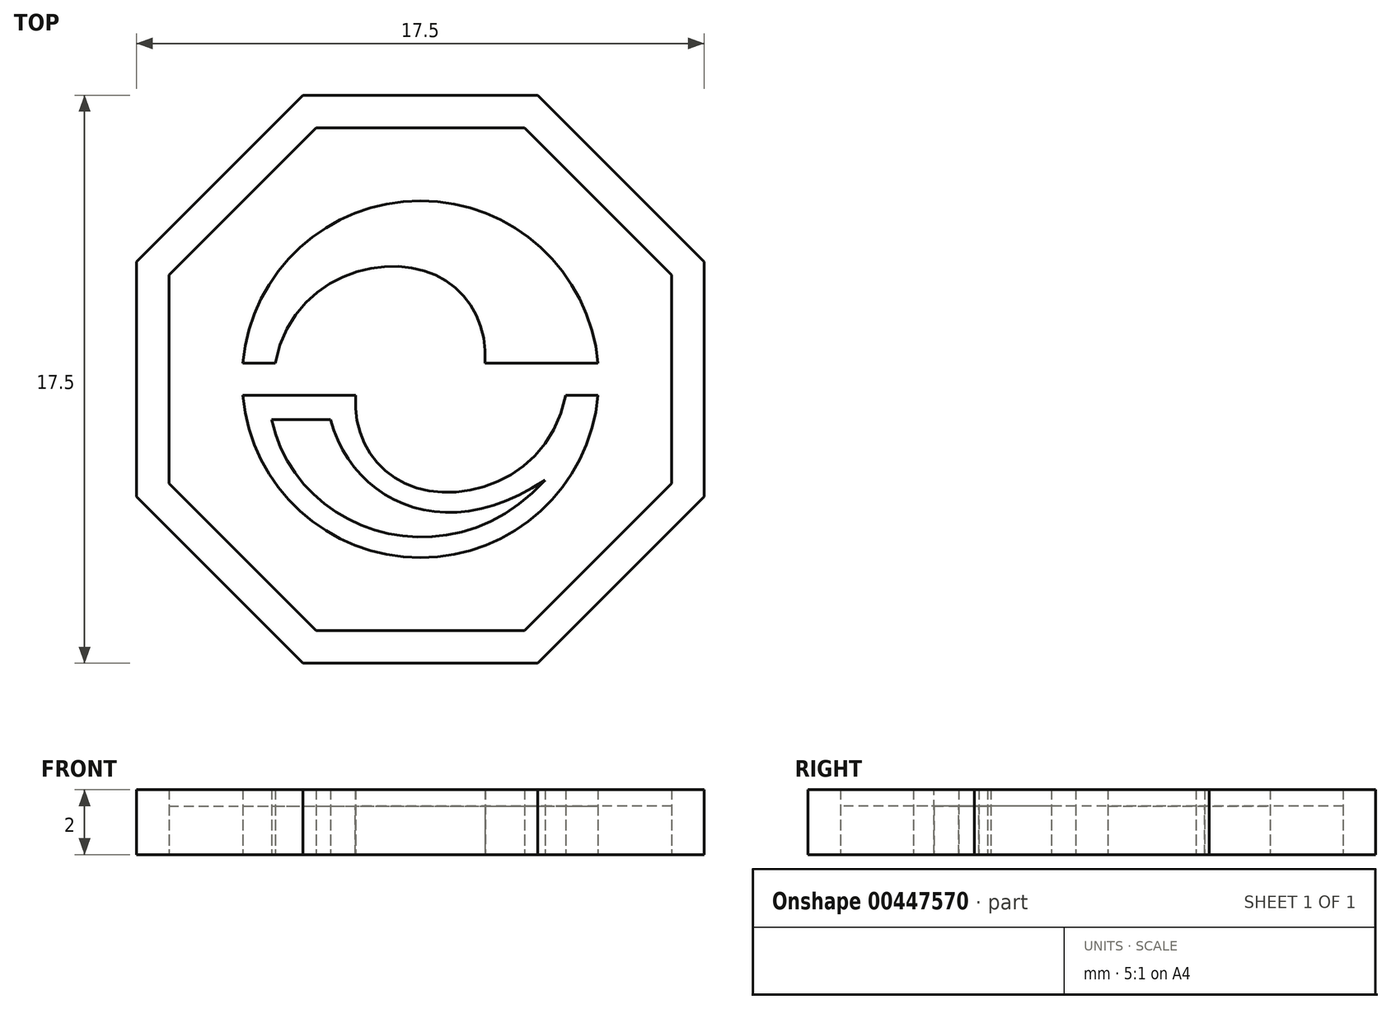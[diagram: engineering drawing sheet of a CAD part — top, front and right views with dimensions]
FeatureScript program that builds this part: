
annotation { "Feature Type Name" : "Feature", "Feature Type Description" : "" }
export const myFeature = defineFeature(function(context is Context, id is Id, definition is map)
    precondition{}
    {
        {
            var Q0;
            Q0=qCreatedBy(makeId("Top.planeOp"),FACE);
            var sketch = newSketch(context, id + "F0", { "sketchPlane" : qUnion([Q0])});
            skArc(sketch, "E0", {"start": v(-5.48, -0.5) * mm, "mid": v(0, -5.5) * mm, "end": v(5.48, -0.5) * mm});
            skLineSegment(sketch, "E1", {"start": v(-5.48, 0.5) * mm, "end": v(-4.48, 0.5) * mm});
            skLineSegment(sketch, "E2", {"start": v(-5.48, -0.5) * mm, "end": v(-2, -0.5) * mm});
            skArc(sketch, "E3.trimOffspring", {"start": v(5.48, 0.5) * mm, "mid": v(0, 5.5) * mm, "end": v(-5.48, 0.5) * mm});
            skPoint(sketch, "E4.2.internal.snap0", {"position": v(0, 0.5) * mm});
            skFitSpline(sketch, "E4", {"points": [v(-4.48, 0.5) * mm, v(0, 3.38) * mm, v(2, 0.5) * mm], "startDerivative": vector(2.69, 13.45) * mm, "endDerivative": vector(-0.52, -9.25) * mm});
            skFitSpline(sketch, "E5", {"points": [v(4.48, -0.5) * mm, v(0, -3.38) * mm, v(-2, -0.5) * mm], "startDerivative": vector(-2.69, -13.45) * mm, "endDerivative": vector(0.52, 9.25) * mm});
            skLineSegment(sketch, "E6.trimOffspring", {"start": v(2, 0.5) * mm, "end": v(5.48, 0.5) * mm});
            skLineSegment(sketch, "E7.trimOffspring", {"start": v(4.48, -0.5) * mm, "end": v(5.48, -0.5) * mm});
            skLineSegment(sketch, "E8", {"start": v(-4.58, -1.25) * mm, "end": v(-2.77, -1.25) * mm});
            skFitSpline(sketch, "E9", {"points": [v(-4.58, -1.25) * mm, v(3.85, -3.1) * mm], "startDerivative": vector(2.26, -10.5) * mm, "endDerivative": vector(8.91, 9.73) * mm});
            skFitSpline(sketch, "E10", {"points": [v(-2.77, -1.25) * mm, v(3.85, -3.1) * mm], "startDerivative": vector(2.08, -7.5) * mm, "endDerivative": vector(9.4, 6.23) * mm});
            skCircle(sketch, "E11.cCircle", {"center": v(0, 0) * mm, "radius": 7.75 * mm, "construction": true});
            skLineSegment(sketch, "E11.0", {"start": v(7.75, -3.21) * mm, "end": v(3.21, -7.75) * mm});
            skLineSegment(sketch, "E11.1", {"start": v(3.21, -7.75) * mm, "end": v(-3.21, -7.75) * mm});
            skLineSegment(sketch, "E11.2", {"start": v(-3.21, -7.75) * mm, "end": v(-7.75, -3.21) * mm});
            skLineSegment(sketch, "E11.3", {"start": v(-7.75, -3.21) * mm, "end": v(-7.75, 3.21) * mm});
            skLineSegment(sketch, "E11.4", {"start": v(-7.75, 3.21) * mm, "end": v(-3.21, 7.75) * mm});
            skLineSegment(sketch, "E11.5", {"start": v(-3.21, 7.75) * mm, "end": v(3.21, 7.75) * mm});
            skLineSegment(sketch, "E11.6", {"start": v(3.21, 7.75) * mm, "end": v(7.75, 3.21) * mm});
            skLineSegment(sketch, "E11.7", {"start": v(7.75, 3.21) * mm, "end": v(7.75, -3.21) * mm});
            skPoint(sketch, "E11.0.midPoint", {"position": v(5.48, -5.48) * mm});
            skCircle(sketch, "E12.cCircle", {"center": v(0, 0) * mm, "radius": 8.75 * mm, "construction": true});
            skLineSegment(sketch, "E12.0", {"start": v(8.75, -3.62) * mm, "end": v(3.62, -8.75) * mm});
            skLineSegment(sketch, "E12.1", {"start": v(3.62, -8.75) * mm, "end": v(-3.62, -8.75) * mm});
            skLineSegment(sketch, "E12.2", {"start": v(-3.62, -8.75) * mm, "end": v(-8.75, -3.62) * mm});
            skLineSegment(sketch, "E12.3", {"start": v(-8.75, -3.62) * mm, "end": v(-8.75, 3.62) * mm});
            skLineSegment(sketch, "E12.4", {"start": v(-8.75, 3.62) * mm, "end": v(-3.62, 8.75) * mm});
            skLineSegment(sketch, "E12.5", {"start": v(-3.62, 8.75) * mm, "end": v(3.62, 8.75) * mm});
            skLineSegment(sketch, "E12.6", {"start": v(3.62, 8.75) * mm, "end": v(8.75, 3.62) * mm});
            skLineSegment(sketch, "E12.7", {"start": v(8.75, 3.62) * mm, "end": v(8.75, -3.62) * mm});
            skPoint(sketch, "E12.0.midPoint", {"position": v(6.19, -6.19) * mm});
            skSolve(sketch);
        }
        {
            var Q0;
            Q0=makeQuery(id+"F0.imprint","IMPRINT",FACE,{"disambiguationData":[TD([[makeQuery(id+"F0.imprint","IMPRINT",EDGE,{"derivedFrom":sQuery(id+"F0.wireOp",EDGE,"62a68324-341a-4806-85d3-5feda647a868")}),1.0]])]});
            var Q1;
            Q1=makeQuery(id+"F0.imprint","IMPRINT",FACE,{"disambiguationData":[TD([[makeQuery(id+"F0.imprint","IMPRINT",EDGE,{"derivedFrom":sQuery(id+"F0.wireOp",EDGE,"E1")}),1.0]])]});
            var Q2;
            Q2=makeQuery(id+"F0.imprint","IMPRINT",FACE,{"disambiguationData":[TD([[makeQuery(id+"F0.imprint","IMPRINT",EDGE,{"derivedFrom":sQuery(id+"F0.wireOp",EDGE,"E0")}),1.0]])]});
            var Q3;
            Q3=makeQuery(id+"F0.imprint","IMPRINT",FACE,{"disambiguationData":[TD([[makeQuery(id+"F0.imprint","IMPRINT",EDGE,{"derivedFrom":sQuery(id+"F0.wireOp",EDGE,"E11.0")}),1.0]])]});
            extrude(context, id + "F1", {"entities" : qUnion([Q0, Q1, Q2, Q3]), "depth" : 2 * mm});
        }
        {
            var Q0;
            Q0=makeQuery(id+"F0.imprint","IMPRINT",FACE,{"disambiguationData":[TD([[makeQuery(id+"F0.imprint","IMPRINT",EDGE,{"derivedFrom":sQuery(id+"F0.wireOp",EDGE,"2e3d32d5-dc82-442d-8b00-b74b8bb0e9ca")}),1.0]])]});
            var Q1;
            Q1=makeQuery(id+"F0.imprint","IMPRINT",FACE,{"disambiguationData":[TD([[makeQuery(id+"F0.imprint","IMPRINT",EDGE,{"derivedFrom":sQuery(id+"F0.wireOp",EDGE,"E8")}),-1.0]])]});
            var Q2;
            Q2=makeQuery(id+"F0.imprint","IMPRINT",FACE,{"disambiguationData":[TD([[makeQuery(id+"F0.imprint","IMPRINT",EDGE,{"derivedFrom":sQuery(id+"F0.wireOp",EDGE,"E0")}),-1.0]])]});
            extrude(context, id + "F2", {"entities" : qUnion([Q0, Q1, Q2]), "depth" : 1.5 * mm});
        }
    });
